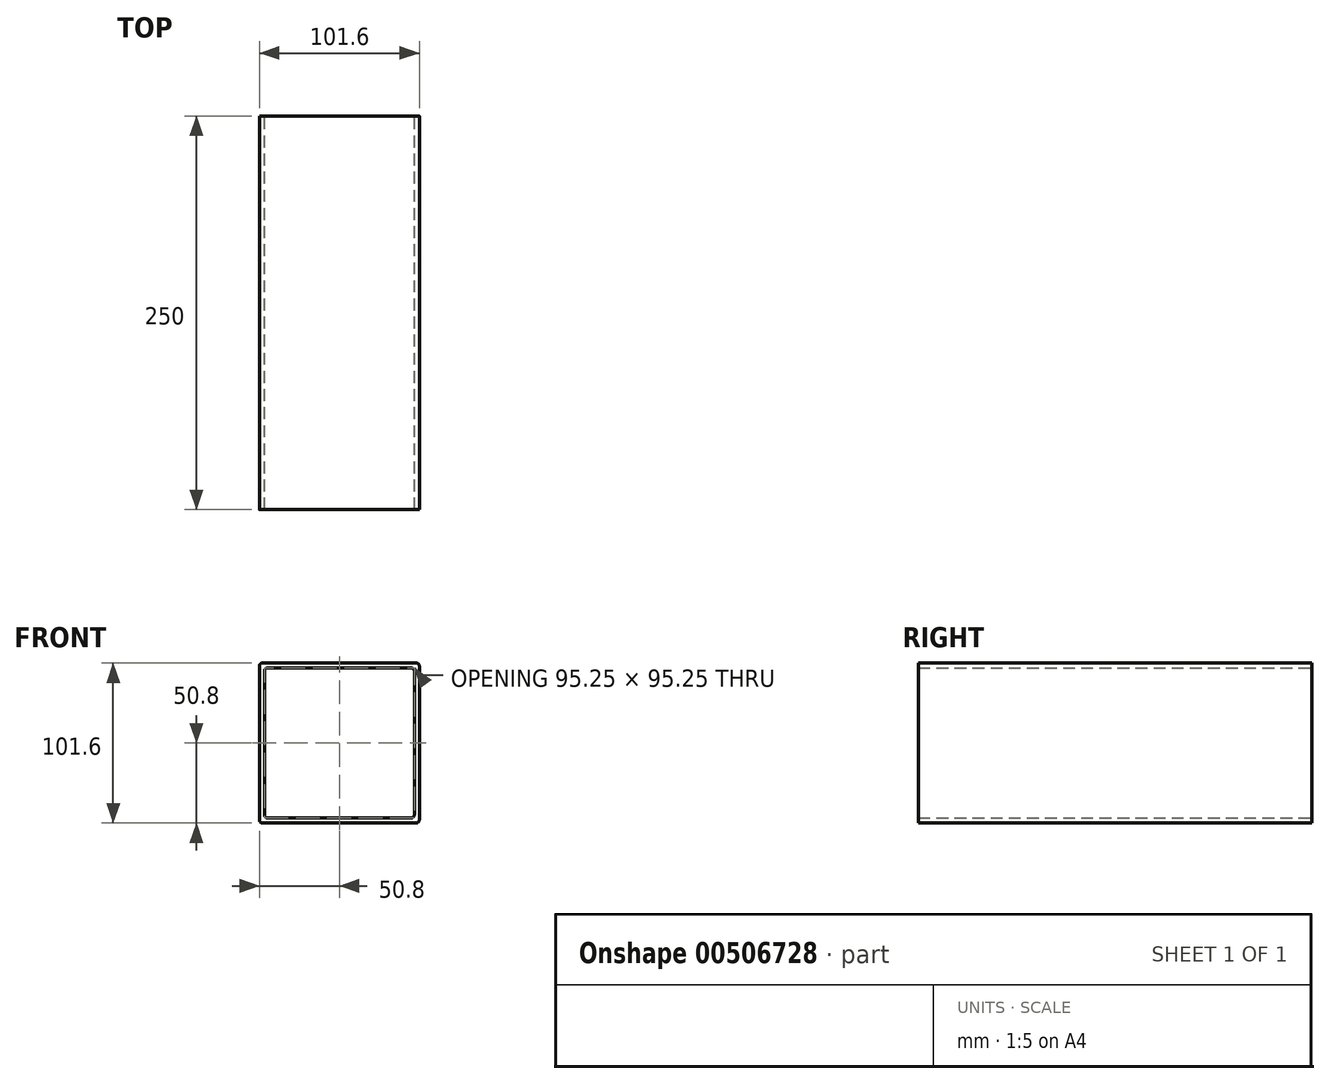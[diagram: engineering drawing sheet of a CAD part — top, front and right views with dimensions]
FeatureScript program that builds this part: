
annotation { "Feature Type Name" : "Feature", "Feature Type Description" : "" }
export const myFeature = defineFeature(function(context is Context, id is Id, definition is map)
    precondition{}
    {
        {
            var Q0;
            Q0=qCreatedBy(makeId("Front.planeOp"),FACE);
            var sketch = newSketch(context, id + "F0", { "sketchPlane" : qUnion([Q0])});
            skLineSegment(sketch, "E0.bottom", {"start": v(48.8, 50.8) * mm, "end": v(-48.8, 50.8) * mm});
            skLineSegment(sketch, "E0.top", {"start": v(48.8, -50.8) * mm, "end": v(-48.8, -50.8) * mm});
            skLineSegment(sketch, "E0.left", {"start": v(50.8, 48.8) * mm, "end": v(50.8, -48.8) * mm});
            skLineSegment(sketch, "E0.right", {"start": v(-50.8, 48.8) * mm, "end": v(-50.8, -48.8) * mm});
            skPoint(sketch, "E0.middle", {"position": v(0, 0) * mm});
            skLineSegment(sketch, "E1.0", {"start": v(-47.62, 45.62) * mm, "end": v(-47.62, -45.62) * mm});
            skLineSegment(sketch, "E1.1", {"start": v(45.62, 47.62) * mm, "end": v(-45.62, 47.62) * mm});
            skLineSegment(sketch, "E1.2", {"start": v(47.63, 45.63) * mm, "end": v(47.62, -45.62) * mm});
            skLineSegment(sketch, "E1.3", {"start": v(45.62, -47.62) * mm, "end": v(-45.62, -47.62) * mm});
            skPoint(sketch, "E2.visualSharp", {"position": v(-50.8, 50.8) * mm});
            skArc(sketch, "E2.filletArc", {"start": v(-48.8, 50.8) * mm, "mid": v(-50.21, 50.21) * mm, "end": v(-50.8, 48.8) * mm});
            skPoint(sketch, "E3.visualSharp", {"position": v(-47.62, 47.62) * mm});
            skArc(sketch, "E3.filletArc", {"start": v(-45.62, 47.62) * mm, "mid": v(-47.04, 47.04) * mm, "end": v(-47.62, 45.62) * mm});
            skPoint(sketch, "E4.visualSharp", {"position": v(47.62, 47.62) * mm});
            skArc(sketch, "E4.filletArc", {"start": v(47.62, 45.62) * mm, "mid": v(47.04, 47.04) * mm, "end": v(45.62, 47.62) * mm});
            skPoint(sketch, "E5.visualSharp", {"position": v(50.8, 50.8) * mm});
            skArc(sketch, "E5.filletArc", {"start": v(50.8, 48.8) * mm, "mid": v(50.21, 50.21) * mm, "end": v(48.8, 50.8) * mm});
            skPoint(sketch, "E6.visualSharp", {"position": v(50.8, -50.8) * mm});
            skArc(sketch, "E6.filletArc", {"start": v(48.8, -50.8) * mm, "mid": v(50.21, -50.21) * mm, "end": v(50.8, -48.8) * mm});
            skPoint(sketch, "E7.visualSharp", {"position": v(47.62, -47.62) * mm});
            skArc(sketch, "E7.filletArc", {"start": v(45.62, -47.63) * mm, "mid": v(47.04, -47.04) * mm, "end": v(47.63, -45.62) * mm});
            skPoint(sketch, "E8.visualSharp", {"position": v(-47.62, -47.62) * mm});
            skArc(sketch, "E8.filletArc", {"start": v(-47.63, -45.62) * mm, "mid": v(-47.04, -47.04) * mm, "end": v(-45.62, -47.63) * mm});
            skPoint(sketch, "E9.visualSharp", {"position": v(-50.8, -50.8) * mm});
            skArc(sketch, "E9.filletArc", {"start": v(-50.8, -48.8) * mm, "mid": v(-50.21, -50.21) * mm, "end": v(-48.8, -50.8) * mm});
            skSolve(sketch);
        }
        {
            var Q0;
            Q0 = qSketchRegion(id + "F0", true);
            extrude(context, id + "F1", {"entities" : qUnion([Q0]), "endBound" : BoundingType.SYMMETRIC, "depth" : 250 * mm, "offsetDistance" : 25 * mm});
        }
    });
